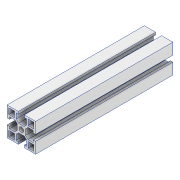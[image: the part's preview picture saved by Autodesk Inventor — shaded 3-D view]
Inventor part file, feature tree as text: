
AUTODESK INVENTOR PART (.ipt)
format: ipt  version: 2020 (Build 240168000, 168)  size: 169,472 bytes
history: native  units: mm
features: other x1, extrude x1, sketch x1
ambient origin geometry x8: Origin, YZ Plane, XZ Plane, XY Plane, X Axis, Y Axis, Z Axis, Center Point
bodies: Body1 (feature_tree)
feature tree (3):
  other  "솔리드1"
  extrude  "돌출1"  Depth=30.0mm
  sketch  "스케치1"
